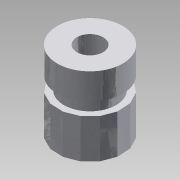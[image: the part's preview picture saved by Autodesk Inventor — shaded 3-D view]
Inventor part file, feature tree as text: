
AUTODESK INVENTOR PART (.ipt)
format: ipt  version: 2015 (Build 190159000, 159)  size: 138,240 bytes
history: native  units: mm
features: extrude x3, sketch x3, projected_geometry x2
ambient origin geometry x8: Origin, YZ Plane, XZ Plane, XY Plane, X Axis, Y Axis, Z Axis, Center Point
bodies: Solid1 (feature_tree)
feature tree (8):
  extrude  "Extrusion1"  Depth=3.0mm TaperAngle=0.0deg
  extrude  "Extrusion2"  Depth=1.0mm TaperAngle=0.0deg
  extrude  "Extrusion3"  Depth=2.0mm TaperAngle=0.0deg
  sketch  "Sketch1"  dims[d1=2.0mm d2=3.0mm d3=0.0mm]
  sketch  "Sketch2"  dims[d4=4.0mm d5=1.0mm d6=0.0mm]
  projected_geometry  "Projected Loop1"
  sketch  "Sketch3"  dims[d7=5.0mm d8=2.0mm d9=0.0mm]
  projected_geometry  "Projected Loop2"
